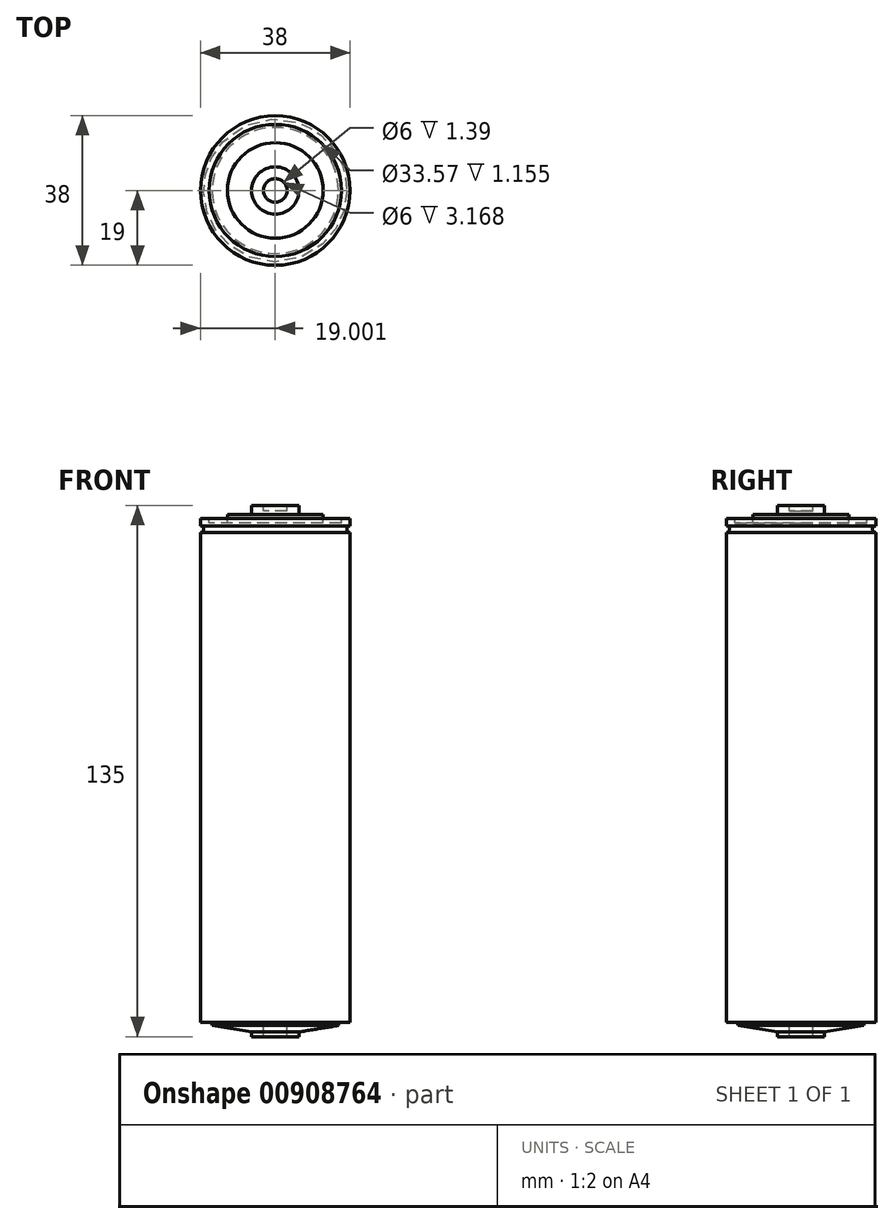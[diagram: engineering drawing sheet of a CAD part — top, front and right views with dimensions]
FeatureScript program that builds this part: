
annotation { "Feature Type Name" : "Feature", "Feature Type Description" : "" }
export const myFeature = defineFeature(function(context is Context, id is Id, definition is map)
    precondition{}
    {
        {
            var Q0;
            Q0=qCreatedBy(makeId("Front.planeOp"),FACE);
            var sketch = newSketch(context, id + "F0", { "sketchPlane" : qUnion([Q0])});
            skLineSegment(sketch, "E0", {"start": v(489.55, 8.97) * mm, "end": v(486.55, 8.97) * mm});
            skLineSegment(sketch, "E1", {"start": v(486.55, 8.97) * mm, "end": v(486.55, 6.66) * mm});
            skLineSegment(sketch, "E2", {"start": v(486.55, 6.66) * mm, "end": v(480.4, 6.66) * mm});
            skLineSegment(sketch, "E3", {"start": v(480.4, 6.66) * mm, "end": v(480.4, 4.44) * mm});
            skLineSegment(sketch, "E4", {"start": v(480.4, 4.44) * mm, "end": v(475.77, 4.44) * mm});
            skLineSegment(sketch, "E5", {"start": v(475.77, 4.44) * mm, "end": v(475.77, 5.6) * mm});
            skLineSegment(sketch, "E6", {"start": v(475.77, 5.6) * mm, "end": v(473.55, 5.6) * mm});
            skLineSegment(sketch, "E7", {"start": v(473.55, 5.6) * mm, "end": v(473.55, 3.77) * mm});
            skLineSegment(sketch, "E8", {"start": v(473.55, 2.1) * mm, "end": v(473.55, -122.36) * mm});
            skLineSegment(sketch, "E9", {"start": v(473.55, -122.36) * mm, "end": v(476.53, -122.36) * mm});
            skArc(sketch, "E10", {"start": v(473.55, 2.1) * mm, "mid": v(474.38, 2.93) * mm, "end": v(473.55, 3.77) * mm});
            skLineSegment(sketch, "E11", {"start": v(492.55, 35.22) * mm, "end": v(492.55, -143.93) * mm});
            skLineSegment(sketch, "E12", {"start": v(489.55, 8.97) * mm, "end": v(489.55, 7.58) * mm});
            skLineSegment(sketch, "E13", {"start": v(489.55, 7.58) * mm, "end": v(492.55, 7.58) * mm});
            skPoint(sketch, "E14.orphan", {"position": v(492.55, 8.97) * mm});
            skPoint(sketch, "E15.end.orphan", {"position": v(492.55, -143.93) * mm});
            skPoint(sketch, "E16.orphan", {"position": v(492.55, -326.61) * mm});
            skLineSegment(sketch, "E17", {"start": v(476.53, -122.36) * mm, "end": v(476.53, -123.2) * mm});
            skLineSegment(sketch, "E18", {"start": v(476.53, -123.2) * mm, "end": v(486.55, -124.83) * mm});
            skLineSegment(sketch, "E19", {"start": v(486.55, -124.83) * mm, "end": v(486.55, -126.03) * mm});
            skLineSegment(sketch, "E20", {"start": v(486.55, -126.03) * mm, "end": v(489.55, -126.03) * mm});
            skLineSegment(sketch, "E21", {"start": v(489.55, -126.03) * mm, "end": v(489.55, -122.86) * mm});
            skLineSegment(sketch, "E22", {"start": v(489.55, -122.86) * mm, "end": v(492.55, -122.86) * mm});
            skSolve(sketch);
        }
        {
            var Q0;
            Q0=makeQuery(id+"F0.imprint","IMPRINT",FACE,{"disambiguationData":[TD([[makeQuery(id+"F0.imprint","IMPRINT",EDGE,{"derivedFrom":sQuery(id+"F0.wireOp",EDGE,"E0")}),1.0]])]});
            var Q1;
            Q1=sQuery(id+"F0.wireOp",EDGE,"E11");
            revolve(context, id + "F1", {"surfaceOperationType" : NewSurfaceOperationType.NEW, "entities" : qUnion([Q0]), "axis" : qUnion([Q1]), "revolveType" : RevolveType.FULL});
        }
    });
